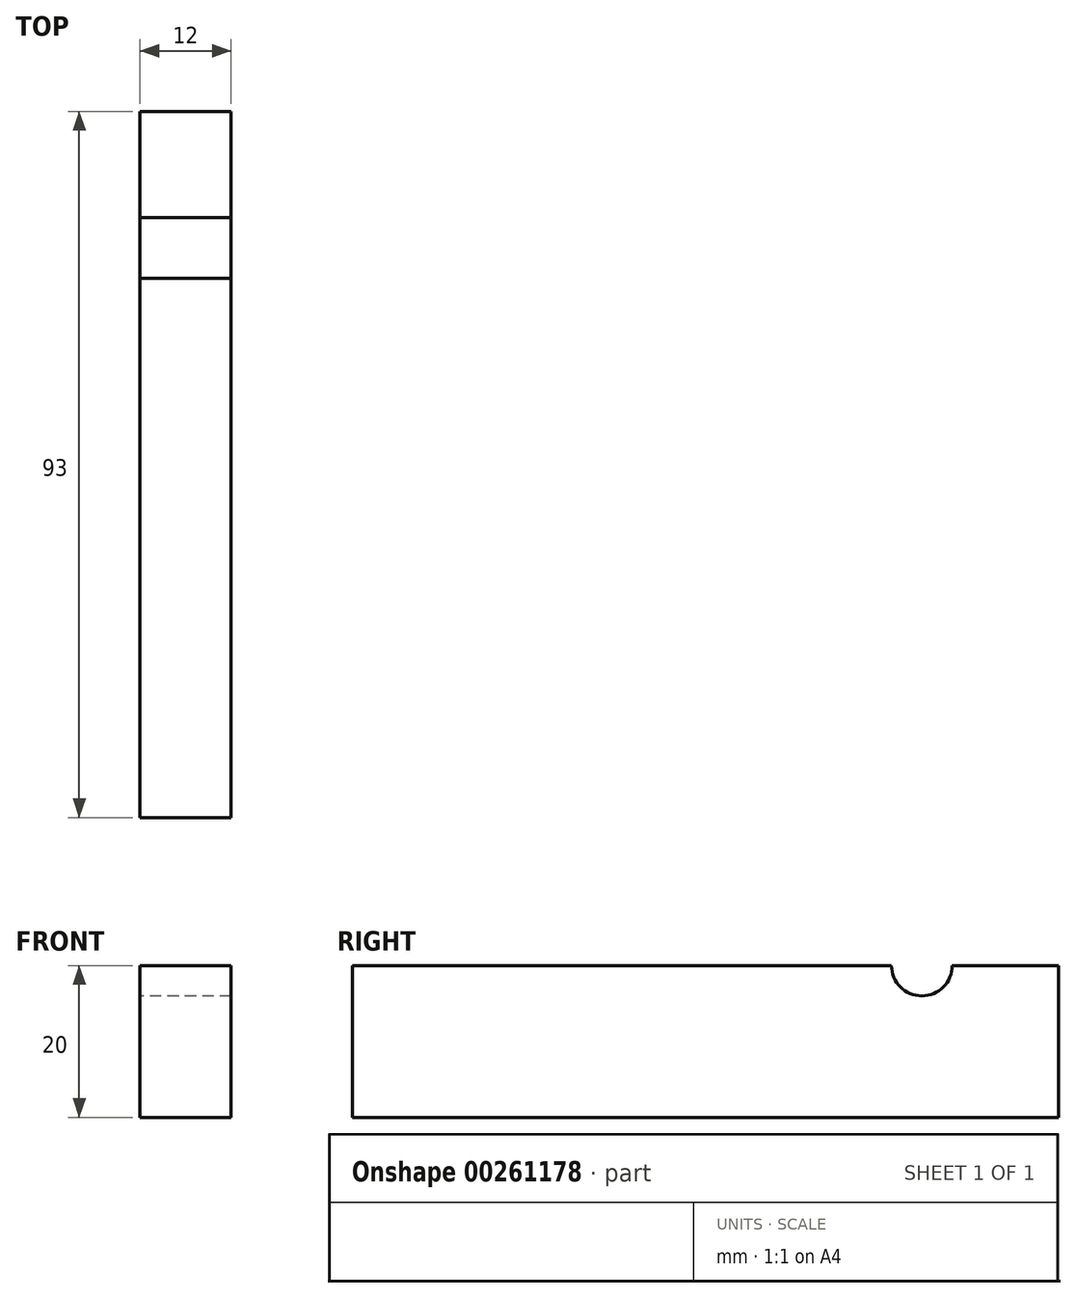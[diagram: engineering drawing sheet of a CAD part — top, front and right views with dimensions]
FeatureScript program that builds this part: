
annotation { "Feature Type Name" : "Feature", "Feature Type Description" : "" }
export const myFeature = defineFeature(function(context is Context, id is Id, definition is map)
    precondition{}
    {
        {
            var Q0;
            Q0=qCreatedBy(makeId("Right.planeOp"),FACE);
            var sketch = newSketch(context, id + "F0", { "sketchPlane" : qUnion([Q0])});
            skLineSegment(sketch, "E0", {"start": v(0, 0) * mm, "end": v(75, 0) * mm});
            skCircle(sketch, "E1", {"center": v(75, 0) * mm, "radius": 4 * mm});
            skArc(sketch, "E2", {"start": v(85, 0) * mm, "mid": v(75, 10) * mm, "end": v(65, 0) * mm});
            skLineSegment(sketch, "E3", {"start": v(75, 0) * mm, "end": v(75, 4) * mm});
            skLineSegment(sketch, "E4", {"start": v(75, 4) * mm, "end": v(57, 4) * mm});
            skLineSegment(sketch, "E5", {"start": v(57, 4) * mm, "end": v(57, 0) * mm});
            skLineSegment(sketch, "E6", {"start": v(75, 4) * mm, "end": v(93, 4) * mm});
            skLineSegment(sketch, "E7", {"start": v(93, 4) * mm, "end": v(93, 0) * mm});
            skLineSegment(sketch, "E8", {"start": v(93, 0) * mm, "end": v(75, 0) * mm});
            skLineSegment(sketch, "E9", {"start": v(0, 0) * mm, "end": v(0, -20) * mm});
            skLineSegment(sketch, "E10", {"start": v(0, -20) * mm, "end": v(93, -20) * mm});
            skLineSegment(sketch, "E11", {"start": v(93, -20) * mm, "end": v(93, 0) * mm});
            skSolve(sketch);
        }
        {
            var Q0;
            {var subQ10=sQuery(id+"F0.wireOp",EDGE,"E9");Q0=makeQuery(id+"F0.imprint","IMPRINT",FACE,{"disambiguationData":[TD([[makeQuery(id+"F0.imprint","IMPRINT",EDGE,{"derivedFrom":subQ10}),1.0]])]});}
            extrude(context, id + "F1", {"entities" : qUnion([Q0]), "depth" : 12 * mm});
        }
    });
